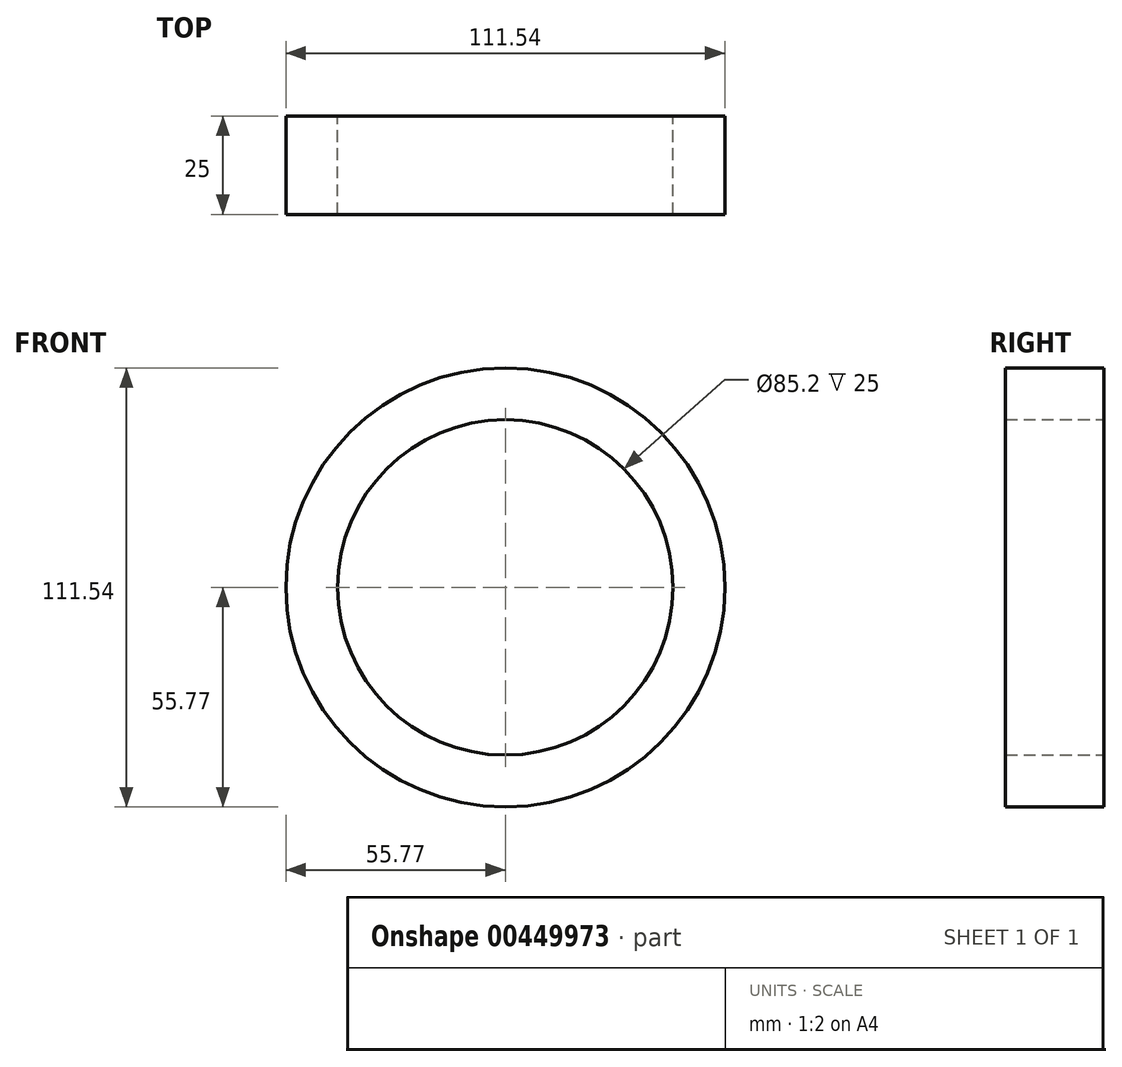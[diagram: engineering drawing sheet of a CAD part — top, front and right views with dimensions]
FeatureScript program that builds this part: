
annotation { "Feature Type Name" : "Feature", "Feature Type Description" : "" }
export const myFeature = defineFeature(function(context is Context, id is Id, definition is map)
    precondition{}
    {
        {
            var Q0;
            Q0=qCreatedBy(makeId("Front.planeOp"),FACE);
            var sketch = newSketch(context, id + "F0", { "sketchPlane" : qUnion([Q0])});
            skCircle(sketch, "E0", {"center": v(0, 0) * mm, "radius": 55.77 * mm});
            skCircle(sketch, "E1", {"center": v(0, 0) * mm, "radius": 42.6 * mm});
            skSolve(sketch);
        }
        {
            var Q0;
            Q0=makeQuery(id+"F0.imprint","IMPRINT",FACE,{"disambiguationData":[TD([[makeQuery(id+"F0.imprint","IMPRINT",EDGE,{"derivedFrom":sQuery(id+"F0.wireOp",EDGE,"E0")}),1.0]])]});
            extrude(context, id + "F1", {"entities" : qUnion([Q0]), "depth" : 25 * mm});
        }
    });
